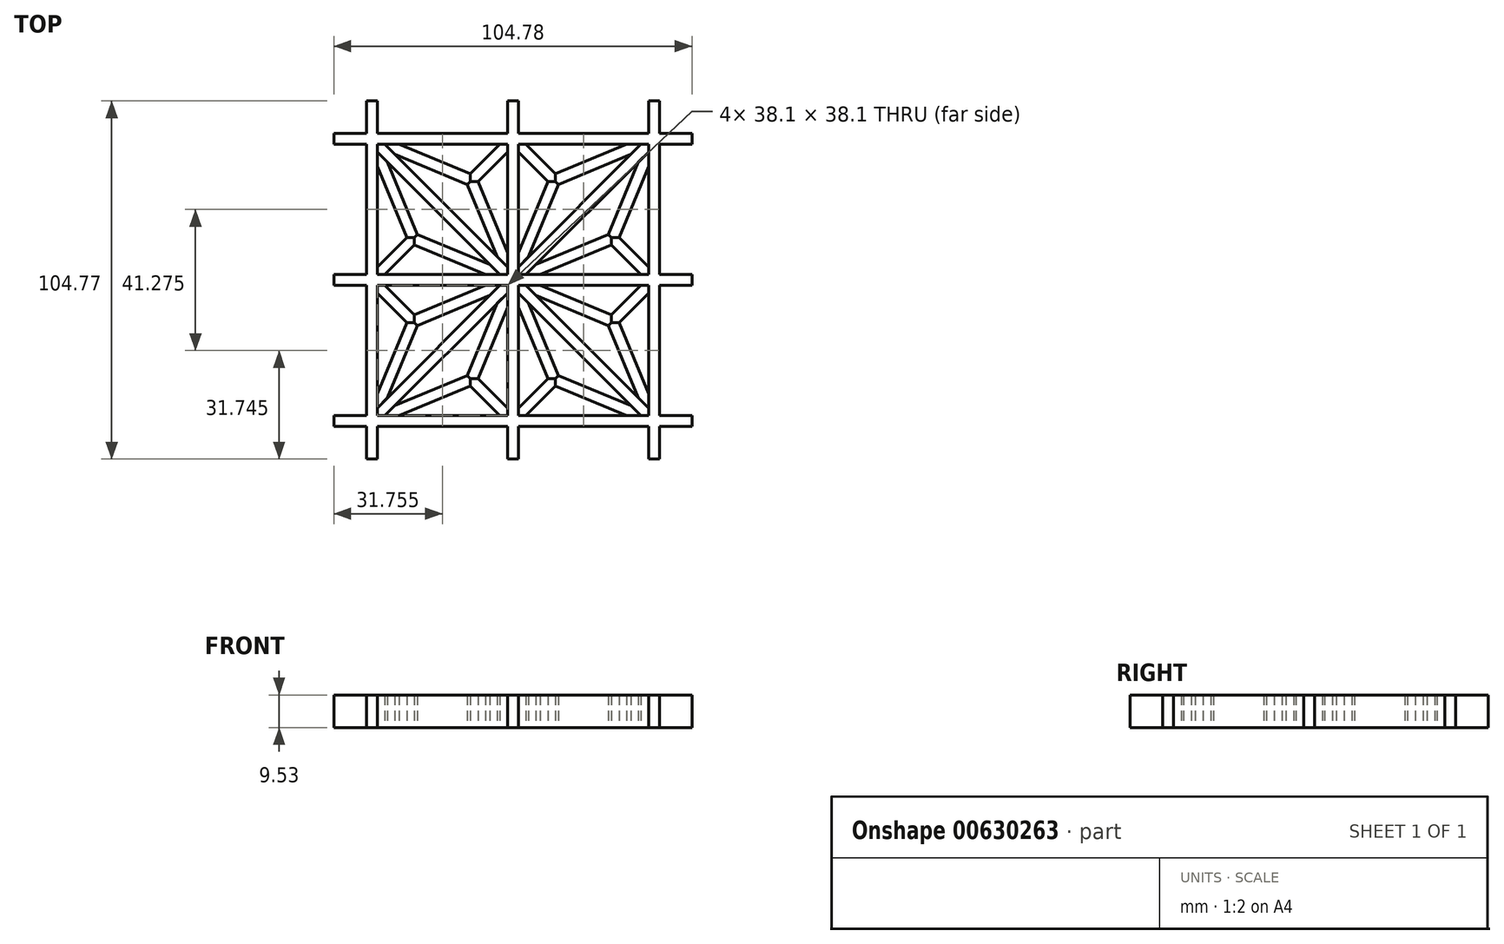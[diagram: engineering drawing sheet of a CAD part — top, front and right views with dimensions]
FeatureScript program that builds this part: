
annotation { "Feature Type Name" : "Feature", "Feature Type Description" : "" }
export const myFeature = defineFeature(function(context is Context, id is Id, definition is map)
    precondition{}
    {
        {
            var Q0;
            Q0=qCreatedBy(makeId("Top.planeOp"),FACE);
            var sketch = newSketch(context, id + "F0", { "sketchPlane" : qUnion([Q0])});
            skLineSegment(sketch, "E0.bottom", {"start": v(0, 0) * mm, "end": v(3.17, 0) * mm});
            skLineSegment(sketch, "E0.top", {"start": v(0, -104.78) * mm, "end": v(3.18, -104.78) * mm});
            skLineSegment(sketch, "E0.left", {"start": v(0, 0) * mm, "end": v(0, -104.78) * mm});
            skLineSegment(sketch, "E0.right", {"start": v(3.17, 0) * mm, "end": v(3.17, -104.78) * mm});
            skLineSegment(sketch, "E1.bottom", {"start": v(41.28, 0) * mm, "end": v(44.45, 0) * mm});
            skLineSegment(sketch, "E1.top", {"start": v(41.28, -104.78) * mm, "end": v(44.45, -104.78) * mm});
            skLineSegment(sketch, "E1.left", {"start": v(41.28, 0) * mm, "end": v(41.28, -104.78) * mm});
            skLineSegment(sketch, "E1.right", {"start": v(44.45, 0) * mm, "end": v(44.45, -104.78) * mm});
            skLineSegment(sketch, "E2.bottom", {"start": v(82.55, 0) * mm, "end": v(85.73, 0) * mm});
            skLineSegment(sketch, "E2.top", {"start": v(82.55, -104.78) * mm, "end": v(85.73, -104.78) * mm});
            skLineSegment(sketch, "E2.left", {"start": v(82.55, 0) * mm, "end": v(82.55, -104.78) * mm});
            skLineSegment(sketch, "E2.right", {"start": v(85.73, 0) * mm, "end": v(85.73, -104.78) * mm});
            skLineSegment(sketch, "E3", {"start": v(3.17, 0) * mm, "end": v(41.28, 0) * mm, "construction": true});
            skLineSegment(sketch, "E4", {"start": v(44.45, 0) * mm, "end": v(82.55, 0) * mm, "construction": true});
            skLineSegment(sketch, "E5", {"start": v(-9.53, -107.95) * mm, "end": v(95.25, -107.95) * mm, "construction": true});
            skLineSegment(sketch, "E6", {"start": v(0, -104.78) * mm, "end": v(-9.53, -104.78) * mm, "construction": true});
            skLineSegment(sketch, "E7", {"start": v(-9.52, -104.78) * mm, "end": v(-9.52, -107.95) * mm, "construction": true});
            skLineSegment(sketch, "E8", {"start": v(95.25, -107.95) * mm, "end": v(95.25, -104.78) * mm, "construction": true});
            skLineSegment(sketch, "E9", {"start": v(95.25, -104.78) * mm, "end": v(85.73, -104.78) * mm, "construction": true});
            skSolve(sketch);
        }
        {
            var Q0;
            Q0 = qSketchRegion(id + "F0", true);
            extrude(context, id + "F1", {"entities" : qUnion([Q0]), "depth" : 9.52 * mm, "offsetDistance" : 25.4 * mm});
        }
        {
            var Q0;
            Q0=makeQuery(id+"F1.opExtrude","SWEPT_FACE",FACE,{"disambiguationData":[OSD([sQuery(id+"F0.wireOp",EDGE,"E2.right")])]});
            var sketch = newSketch(context, id + "F2", { "sketchPlane" : qUnion([Q0])});
            skLineSegment(sketch, "E10.bottom", {"start": v(-95.25, 0) * mm, "end": v(-92.08, 0) * mm});
            skLineSegment(sketch, "E10.top", {"start": v(-95.25, 4.76) * mm, "end": v(-92.08, 4.76) * mm});
            skLineSegment(sketch, "E10.left", {"start": v(-95.25, 0) * mm, "end": v(-95.25, 4.76) * mm});
            skLineSegment(sketch, "E10.right", {"start": v(-92.08, 0) * mm, "end": v(-92.08, 4.76) * mm});
            skLineSegment(sketch, "E11.bottom", {"start": v(-53.98, 0) * mm, "end": v(-50.8, 0) * mm});
            skLineSegment(sketch, "E11.top", {"start": v(-53.98, 4.76) * mm, "end": v(-50.8, 4.76) * mm});
            skLineSegment(sketch, "E11.left", {"start": v(-50.8, 0) * mm, "end": v(-50.8, 4.76) * mm});
            skLineSegment(sketch, "E11.right", {"start": v(-53.98, 0) * mm, "end": v(-53.98, 4.76) * mm});
            skLineSegment(sketch, "E12.bottom", {"start": v(-12.7, 0) * mm, "end": v(-9.53, 0) * mm});
            skLineSegment(sketch, "E12.top", {"start": v(-12.7, 4.76) * mm, "end": v(-9.53, 4.76) * mm});
            skLineSegment(sketch, "E12.left", {"start": v(-12.7, 0) * mm, "end": v(-12.7, 4.76) * mm});
            skLineSegment(sketch, "E12.right", {"start": v(-9.53, 0) * mm, "end": v(-9.53, 4.76) * mm});
            skLineSegment(sketch, "E13", {"start": v(-52.39, 4.76) * mm, "end": v(-52.39, 9.52) * mm, "construction": true});
            skSolve(sketch);
        }
        {
            var Q0;
            Q0 = qSketchRegion(id + "F2", true);
            extrude(context, id + "F3", {"entities" : qUnion([Q0]), "operationType" : NewBodyOperationType.REMOVE, "endBound" : BoundingType.THROUGH_ALL, "oppositeDirection" : true, "depth" : 25.4 * mm, "offsetDistance" : 25.4 * mm});
        }
        {
            var Q0;
            Q0=qCreatedBy(makeId("Top.planeOp"),FACE);
            var sketch = newSketch(context, id + "F4", { "sketchPlane" : qUnion([Q0])});
            skLineSegment(sketch, "E14.bottom", {"start": v(95.25, -12.7) * mm, "end": v(-9.53, -12.7) * mm});
            skLineSegment(sketch, "E14.top", {"start": v(95.25, -9.53) * mm, "end": v(-9.53, -9.53) * mm});
            skLineSegment(sketch, "E14.left", {"start": v(95.25, -12.7) * mm, "end": v(95.25, -9.53) * mm});
            skLineSegment(sketch, "E14.right", {"start": v(-9.53, -12.7) * mm, "end": v(-9.53, -9.53) * mm});
            skLineSegment(sketch, "E15.bottom", {"start": v(95.25, -53.98) * mm, "end": v(-9.53, -53.98) * mm});
            skLineSegment(sketch, "E15.top", {"start": v(95.25, -50.8) * mm, "end": v(-9.53, -50.8) * mm});
            skLineSegment(sketch, "E15.left", {"start": v(95.25, -53.98) * mm, "end": v(95.25, -50.8) * mm});
            skLineSegment(sketch, "E15.right", {"start": v(-9.52, -53.98) * mm, "end": v(-9.52, -50.8) * mm});
            skLineSegment(sketch, "E16.bottom", {"start": v(95.25, -95.25) * mm, "end": v(-9.53, -95.25) * mm});
            skLineSegment(sketch, "E16.top", {"start": v(95.25, -92.08) * mm, "end": v(-9.53, -92.08) * mm});
            skLineSegment(sketch, "E16.left", {"start": v(95.25, -95.25) * mm, "end": v(95.25, -92.08) * mm});
            skLineSegment(sketch, "E16.right", {"start": v(-9.52, -95.25) * mm, "end": v(-9.52, -92.08) * mm});
            skLineSegment(sketch, "E17", {"start": v(42.86, -9.53) * mm, "end": v(42.86, 0) * mm, "construction": true});
            skSolve(sketch);
        }
        {
            var Q0;
            Q0 = qSketchRegion(id + "F4", true);
            var Q1;
            Q1=makeQuery(id+"F3.boolean.opBoolean","COPY",FACE,{"disambiguationData":[TD([makeQuery(id+"F1.opExtrude","SWEPT_FACE",FACE,{"disambiguationData":[OSD([sQuery(id+"F0.wireOp",EDGE,"E1.left")])]})])],"derivedFrom":makeQuery(id+"F3.opExtrude","SWEPT_FACE",FACE,{"disambiguationData":[OSD([sQuery(id+"F2.wireOp",EDGE,"E12.top")])]})});
            extrude(context, id + "F5", {"entities" : qUnion([Q0]), "endBound" : BoundingType.UP_TO_SURFACE, "depth" : 25.4 * mm, "endBoundEntityFace" : qUnion([Q1]), "offsetDistance" : 25.4 * mm});
        }
        {
            var Q0;
            Q0=makeQuery(id+"F5.opExtrude","CAP_FACE",FACE,{"disambiguationData":[OSD([sQuery(id+"F4.wireOp",EDGE,"E14.bottom"),sQuery(id+"F4.wireOp",EDGE,"E14.top"),sQuery(id+"F4.wireOp",EDGE,"E14.left"),sQuery(id+"F4.wireOp",EDGE,"E14.right")])],"isStart":false});
            var sketch = newSketch(context, id + "F6", { "sketchPlane" : qUnion([Q0])});
            skLineSegment(sketch, "E18.bottom", {"start": v(3.18, -9.53) * mm, "end": v(41.28, -9.53) * mm});
            skLineSegment(sketch, "E18.top", {"start": v(3.18, -12.7) * mm, "end": v(41.28, -12.7) * mm});
            skLineSegment(sketch, "E18.left", {"start": v(3.17, -9.53) * mm, "end": v(3.17, -12.7) * mm});
            skLineSegment(sketch, "E18.right", {"start": v(41.28, -9.53) * mm, "end": v(41.28, -12.7) * mm});
            skLineSegment(sketch, "E19.bottom", {"start": v(3.18, -50.8) * mm, "end": v(41.28, -50.8) * mm});
            skLineSegment(sketch, "E19.top", {"start": v(3.18, -53.98) * mm, "end": v(41.28, -53.98) * mm});
            skLineSegment(sketch, "E19.left", {"start": v(3.17, -50.8) * mm, "end": v(3.17, -53.98) * mm});
            skLineSegment(sketch, "E19.right", {"start": v(41.28, -50.8) * mm, "end": v(41.28, -53.98) * mm});
            skLineSegment(sketch, "E20.bottom", {"start": v(3.18, -92.08) * mm, "end": v(41.28, -92.08) * mm});
            skLineSegment(sketch, "E20.top", {"start": v(3.18, -95.25) * mm, "end": v(41.28, -95.25) * mm});
            skLineSegment(sketch, "E20.left", {"start": v(3.17, -92.08) * mm, "end": v(3.17, -95.25) * mm});
            skLineSegment(sketch, "E20.right", {"start": v(41.28, -92.08) * mm, "end": v(41.28, -95.25) * mm});
            skLineSegment(sketch, "E21.bottom", {"start": v(82.55, -95.25) * mm, "end": v(44.45, -95.25) * mm});
            skLineSegment(sketch, "E21.top", {"start": v(82.55, -92.08) * mm, "end": v(44.45, -92.08) * mm});
            skLineSegment(sketch, "E21.left", {"start": v(82.55, -95.25) * mm, "end": v(82.55, -92.08) * mm});
            skLineSegment(sketch, "E21.right", {"start": v(44.45, -95.25) * mm, "end": v(44.45, -92.08) * mm});
            skLineSegment(sketch, "E22.bottom", {"start": v(82.55, -53.98) * mm, "end": v(44.45, -53.98) * mm});
            skLineSegment(sketch, "E22.top", {"start": v(82.55, -50.8) * mm, "end": v(44.45, -50.8) * mm});
            skLineSegment(sketch, "E22.left", {"start": v(82.55, -53.98) * mm, "end": v(82.55, -50.8) * mm});
            skLineSegment(sketch, "E22.right", {"start": v(44.45, -53.98) * mm, "end": v(44.45, -50.8) * mm});
            skLineSegment(sketch, "E23.bottom", {"start": v(82.55, -9.53) * mm, "end": v(44.45, -9.53) * mm});
            skLineSegment(sketch, "E23.top", {"start": v(82.55, -12.7) * mm, "end": v(44.45, -12.7) * mm});
            skLineSegment(sketch, "E23.left", {"start": v(82.55, -9.53) * mm, "end": v(82.55, -12.7) * mm});
            skLineSegment(sketch, "E23.right", {"start": v(44.45, -9.53) * mm, "end": v(44.45, -12.7) * mm});
            skLineSegment(sketch, "E24.bottom", {"start": v(95.25, -9.53) * mm, "end": v(85.73, -9.53) * mm});
            skLineSegment(sketch, "E24.top", {"start": v(95.25, -12.7) * mm, "end": v(85.73, -12.7) * mm});
            skLineSegment(sketch, "E24.left", {"start": v(95.25, -9.53) * mm, "end": v(95.25, -12.7) * mm});
            skLineSegment(sketch, "E24.right", {"start": v(85.73, -9.53) * mm, "end": v(85.73, -12.7) * mm});
            skLineSegment(sketch, "E25.bottom", {"start": v(95.25, -50.8) * mm, "end": v(85.73, -50.8) * mm});
            skLineSegment(sketch, "E25.top", {"start": v(95.25, -53.98) * mm, "end": v(85.73, -53.98) * mm});
            skLineSegment(sketch, "E25.left", {"start": v(95.25, -50.8) * mm, "end": v(95.25, -53.98) * mm});
            skLineSegment(sketch, "E25.right", {"start": v(85.73, -50.8) * mm, "end": v(85.73, -53.98) * mm});
            skLineSegment(sketch, "E26.bottom", {"start": v(95.25, -92.08) * mm, "end": v(85.73, -92.08) * mm});
            skLineSegment(sketch, "E26.top", {"start": v(95.25, -95.25) * mm, "end": v(85.73, -95.25) * mm});
            skLineSegment(sketch, "E26.left", {"start": v(95.25, -92.08) * mm, "end": v(95.25, -95.25) * mm});
            skLineSegment(sketch, "E26.right", {"start": v(85.73, -92.08) * mm, "end": v(85.73, -95.25) * mm});
            skLineSegment(sketch, "E27.bottom", {"start": v(0, -92.08) * mm, "end": v(-9.52, -92.08) * mm});
            skLineSegment(sketch, "E27.top", {"start": v(0, -95.25) * mm, "end": v(-9.52, -95.25) * mm});
            skLineSegment(sketch, "E27.left", {"start": v(0, -92.08) * mm, "end": v(0, -95.25) * mm});
            skLineSegment(sketch, "E27.right", {"start": v(-9.52, -92.08) * mm, "end": v(-9.52, -95.25) * mm});
            skLineSegment(sketch, "E28.bottom", {"start": v(0, -50.8) * mm, "end": v(-9.52, -50.8) * mm});
            skLineSegment(sketch, "E28.top", {"start": v(0, -53.98) * mm, "end": v(-9.52, -53.98) * mm});
            skLineSegment(sketch, "E28.left", {"start": v(0, -50.8) * mm, "end": v(0, -53.98) * mm});
            skLineSegment(sketch, "E28.right", {"start": v(-9.52, -50.8) * mm, "end": v(-9.52, -53.98) * mm});
            skLineSegment(sketch, "E29.bottom", {"start": v(0, -9.53) * mm, "end": v(-9.53, -9.53) * mm});
            skLineSegment(sketch, "E29.top", {"start": v(0, -12.7) * mm, "end": v(-9.53, -12.7) * mm});
            skLineSegment(sketch, "E29.left", {"start": v(0, -9.53) * mm, "end": v(0, -12.7) * mm});
            skLineSegment(sketch, "E29.right", {"start": v(-9.53, -9.53) * mm, "end": v(-9.53, -12.7) * mm});
            skSolve(sketch);
        }
        {
            var Q0;
            Q0 = qSketchRegion(id + "F6", true);
            var Q1;
            Q1=makeQuery(id+"F1.opExtrude","CAP_FACE",FACE,{"disambiguationData":[OSD([sQuery(id+"F0.wireOp",EDGE,"E1.bottom"),sQuery(id+"F0.wireOp",EDGE,"E1.top"),sQuery(id+"F0.wireOp",EDGE,"E1.left"),sQuery(id+"F0.wireOp",EDGE,"E1.right")])],"isStart":false});
            extrude(context, id + "F7", {"entities" : qUnion([Q0]), "operationType" : NewBodyOperationType.ADD, "endBound" : BoundingType.UP_TO_SURFACE, "depth" : 25.4 * mm, "endBoundEntityFace" : qUnion([Q1]), "offsetDistance" : 25.4 * mm});
        }
        {
            var Q0;
            Q0=qCreatedBy(makeId("Top.planeOp"),FACE);
            var sketch = newSketch(context, id + "F8", { "sketchPlane" : qUnion([Q0])});
            skLineSegment(sketch, "E30", {"start": v(46.7, -53.98) * mm, "end": v(44.45, -53.98) * mm});
            skLineSegment(sketch, "E31", {"start": v(44.45, -53.98) * mm, "end": v(44.45, -56.22) * mm});
            skLineSegment(sketch, "E32", {"start": v(44.45, -56.22) * mm, "end": v(80.3, -92.08) * mm});
            skLineSegment(sketch, "E33", {"start": v(80.3, -92.08) * mm, "end": v(82.55, -92.08) * mm});
            skLineSegment(sketch, "E34", {"start": v(82.55, -14.95) * mm, "end": v(46.7, -50.8) * mm});
            skLineSegment(sketch, "E35", {"start": v(46.7, -50.8) * mm, "end": v(44.45, -50.8) * mm});
            skLineSegment(sketch, "E36", {"start": v(44.45, -50.8) * mm, "end": v(44.45, -48.55) * mm});
            skLineSegment(sketch, "E37", {"start": v(44.45, -48.55) * mm, "end": v(80.3, -12.7) * mm});
            skLineSegment(sketch, "E38", {"start": v(80.3, -12.7) * mm, "end": v(82.55, -12.7) * mm});
            skLineSegment(sketch, "E39", {"start": v(82.55, -12.7) * mm, "end": v(82.55, -14.95) * mm});
            skLineSegment(sketch, "E40", {"start": v(41.28, -50.8) * mm, "end": v(41.28, -48.55) * mm});
            skLineSegment(sketch, "E41", {"start": v(41.28, -48.55) * mm, "end": v(5.42, -12.7) * mm});
            skLineSegment(sketch, "E42", {"start": v(5.42, -12.7) * mm, "end": v(3.17, -12.7) * mm});
            skLineSegment(sketch, "E43", {"start": v(3.17, -12.7) * mm, "end": v(3.17, -14.95) * mm});
            skLineSegment(sketch, "E44", {"start": v(3.17, -14.95) * mm, "end": v(39.03, -50.8) * mm});
            skLineSegment(sketch, "E45", {"start": v(39.03, -50.8) * mm, "end": v(41.28, -50.8) * mm});
            skLineSegment(sketch, "E46", {"start": v(41.28, -56.22) * mm, "end": v(41.28, -53.98) * mm});
            skLineSegment(sketch, "E47", {"start": v(41.28, -53.98) * mm, "end": v(39.03, -53.98) * mm});
            skLineSegment(sketch, "E48", {"start": v(39.03, -53.97) * mm, "end": v(3.17, -89.83) * mm});
            skLineSegment(sketch, "E49", {"start": v(3.17, -89.83) * mm, "end": v(3.18, -92.08) * mm});
            skLineSegment(sketch, "E50", {"start": v(3.18, -92.08) * mm, "end": v(5.42, -92.08) * mm});
            skLineSegment(sketch, "E51", {"start": v(5.42, -92.08) * mm, "end": v(41.28, -56.22) * mm});
            skLineSegment(sketch, "E52", {"start": v(82.55, -92.08) * mm, "end": v(82.55, -89.83) * mm});
            skLineSegment(sketch, "E53", {"start": v(82.55, -89.83) * mm, "end": v(46.7, -53.97) * mm});
            skSolve(sketch);
        }
        {
            var Q0;
            Q0 = qSketchRegion(id + "F8", true);
            var Q1;
            Q1=makeQuery(id+"F1.opExtrude","CAP_FACE",FACE,{"disambiguationData":[OSD([sQuery(id+"F0.wireOp",EDGE,"E1.bottom"),sQuery(id+"F0.wireOp",EDGE,"E1.top"),sQuery(id+"F0.wireOp",EDGE,"E1.left"),sQuery(id+"F0.wireOp",EDGE,"E1.right")])],"isStart":false});
            extrude(context, id + "F9", {"entities" : qUnion([Q0]), "endBound" : BoundingType.UP_TO_SURFACE, "depth" : 25.4 * mm, "endBoundEntityFace" : qUnion([Q1]), "offsetDistance" : 25.4 * mm});
        }
        {
            var Q0;
            Q0=qCreatedBy(makeId("Top.planeOp"),FACE);
            var sketch = newSketch(context, id + "F10", { "sketchPlane" : qUnion([Q0])});
            skLineSegment(sketch, "E54", {"start": v(46.7, -12.7) * mm, "end": v(55.32, -21.33) * mm});
            skLineSegment(sketch, "E55", {"start": v(55.32, -21.33) * mm, "end": v(55.32, -23.57) * mm});
            skLineSegment(sketch, "E56", {"start": v(55.32, -23.57) * mm, "end": v(53.08, -23.57) * mm});
            skLineSegment(sketch, "E57", {"start": v(53.08, -23.57) * mm, "end": v(44.45, -14.95) * mm});
            skLineSegment(sketch, "E58", {"start": v(44.45, -14.95) * mm, "end": v(44.45, -12.7) * mm});
            skLineSegment(sketch, "E59", {"start": v(44.45, -12.7) * mm, "end": v(46.7, -12.7) * mm});
            skLineSegment(sketch, "E60", {"start": v(73.92, -39.93) * mm, "end": v(82.55, -48.55) * mm});
            skLineSegment(sketch, "E61", {"start": v(82.55, -48.55) * mm, "end": v(82.55, -50.8) * mm});
            skLineSegment(sketch, "E62", {"start": v(82.55, -50.8) * mm, "end": v(80.3, -50.8) * mm});
            skLineSegment(sketch, "E63", {"start": v(80.3, -50.8) * mm, "end": v(71.68, -42.17) * mm});
            skLineSegment(sketch, "E64", {"start": v(71.68, -42.17) * mm, "end": v(71.68, -39.93) * mm});
            skLineSegment(sketch, "E65", {"start": v(71.68, -39.93) * mm, "end": v(73.92, -39.93) * mm});
            skLineSegment(sketch, "E66", {"start": v(55.32, -23.57) * mm, "end": v(56.17, -24.42) * mm});
            skLineSegment(sketch, "E67", {"start": v(71.68, -39.93) * mm, "end": v(70.83, -39.08) * mm});
            skLineSegment(sketch, "E68", {"start": v(47.38, -45.62) * mm, "end": v(44.45, -48.55) * mm});
            skLineSegment(sketch, "E69", {"start": v(44.45, -48.55) * mm, "end": v(44.45, -44.4) * mm});
            skLineSegment(sketch, "E70", {"start": v(80.3, -12.7) * mm, "end": v(76.16, -12.7) * mm});
            skLineSegment(sketch, "E71", {"start": v(77.37, -15.63) * mm, "end": v(80.3, -12.7) * mm});
            skLineSegment(sketch, "E72", {"start": v(56.17, -24.42) * mm, "end": v(47.38, -45.62) * mm});
            skLineSegment(sketch, "E73", {"start": v(53.08, -23.57) * mm, "end": v(44.45, -44.4) * mm});
            skLineSegment(sketch, "E74", {"start": v(56.17, -24.42) * mm, "end": v(77.37, -15.63) * mm});
            skLineSegment(sketch, "E75", {"start": v(76.16, -12.7) * mm, "end": v(55.32, -21.33) * mm});
            skLineSegment(sketch, "E76", {"start": v(47.38, -41.47) * mm, "end": v(50.32, -42.69) * mm, "construction": true});
            skLineSegment(sketch, "E77", {"start": v(47.38, -41.47) * mm, "end": v(44.45, -40.26) * mm, "construction": true});
            skLineSegment(sketch, "E78", {"start": v(47.38, -45.62) * mm, "end": v(47.38, -41.47) * mm, "construction": true});
            skLineSegment(sketch, "E79", {"start": v(47.38, -41.47) * mm, "end": v(44.45, -44.4) * mm, "construction": true});
            skLineSegment(sketch, "E80", {"start": v(70.83, -39.08) * mm, "end": v(49.63, -47.87) * mm});
            skLineSegment(sketch, "E81", {"start": v(49.63, -47.87) * mm, "end": v(46.7, -50.8) * mm});
            skLineSegment(sketch, "E82", {"start": v(46.7, -50.8) * mm, "end": v(50.84, -50.8) * mm});
            skLineSegment(sketch, "E83", {"start": v(50.84, -50.8) * mm, "end": v(71.68, -42.17) * mm});
            skLineSegment(sketch, "E84", {"start": v(70.83, -39.08) * mm, "end": v(79.62, -17.88) * mm});
            skLineSegment(sketch, "E85", {"start": v(79.62, -17.88) * mm, "end": v(82.55, -14.95) * mm});
            skLineSegment(sketch, "E86", {"start": v(82.55, -14.95) * mm, "end": v(82.55, -19.1) * mm});
            skLineSegment(sketch, "E87", {"start": v(82.55, -19.1) * mm, "end": v(73.92, -39.93) * mm});
            skLineSegment(sketch, "E88", {"start": v(5.42, -53.97) * mm, "end": v(14.05, -62.6) * mm});
            skLineSegment(sketch, "E89", {"start": v(14.05, -62.6) * mm, "end": v(14.05, -64.85) * mm});
            skLineSegment(sketch, "E90", {"start": v(14.05, -64.85) * mm, "end": v(11.8, -64.85) * mm});
            skLineSegment(sketch, "E91", {"start": v(11.8, -64.85) * mm, "end": v(3.17, -56.22) * mm});
            skLineSegment(sketch, "E92", {"start": v(3.17, -56.22) * mm, "end": v(3.17, -53.98) * mm});
            skLineSegment(sketch, "E93", {"start": v(3.17, -53.97) * mm, "end": v(5.42, -53.97) * mm});
            skLineSegment(sketch, "E94", {"start": v(32.65, -81.2) * mm, "end": v(41.27, -89.83) * mm});
            skLineSegment(sketch, "E95", {"start": v(41.28, -89.83) * mm, "end": v(41.28, -92.08) * mm});
            skLineSegment(sketch, "E96", {"start": v(41.28, -92.08) * mm, "end": v(39.03, -92.08) * mm});
            skLineSegment(sketch, "E97", {"start": v(39.03, -92.08) * mm, "end": v(30.4, -83.45) * mm});
            skLineSegment(sketch, "E98", {"start": v(30.4, -83.45) * mm, "end": v(30.4, -81.2) * mm});
            skLineSegment(sketch, "E99", {"start": v(30.4, -81.2) * mm, "end": v(32.65, -81.2) * mm});
            skLineSegment(sketch, "E100", {"start": v(14.05, -64.85) * mm, "end": v(14.9, -65.7) * mm});
            skLineSegment(sketch, "E101", {"start": v(30.4, -81.2) * mm, "end": v(29.56, -80.36) * mm});
            skLineSegment(sketch, "E102", {"start": v(6.1, -86.9) * mm, "end": v(3.18, -89.83) * mm});
            skLineSegment(sketch, "E103", {"start": v(3.17, -89.83) * mm, "end": v(3.17, -85.68) * mm});
            skLineSegment(sketch, "E104", {"start": v(39.03, -53.98) * mm, "end": v(34.88, -53.98) * mm});
            skLineSegment(sketch, "E105", {"start": v(36.1, -56.9) * mm, "end": v(39.03, -53.98) * mm});
            skLineSegment(sketch, "E106", {"start": v(14.9, -65.7) * mm, "end": v(6.1, -86.9) * mm});
            skLineSegment(sketch, "E107", {"start": v(11.8, -64.85) * mm, "end": v(3.18, -85.68) * mm});
            skLineSegment(sketch, "E108", {"start": v(14.9, -65.7) * mm, "end": v(36.1, -56.9) * mm});
            skLineSegment(sketch, "E109", {"start": v(34.88, -53.98) * mm, "end": v(14.05, -62.6) * mm});
            skLineSegment(sketch, "E110", {"start": v(6.1, -86.9) * mm, "end": v(6.1, -82.75) * mm, "construction": true});
            skLineSegment(sketch, "E111", {"start": v(6.1, -82.75) * mm, "end": v(3.17, -85.68) * mm, "construction": true});
            skLineSegment(sketch, "E112", {"start": v(29.56, -80.36) * mm, "end": v(8.35, -89.14) * mm});
            skLineSegment(sketch, "E113", {"start": v(8.35, -89.14) * mm, "end": v(5.42, -92.08) * mm});
            skLineSegment(sketch, "E114", {"start": v(5.42, -92.08) * mm, "end": v(9.57, -92.08) * mm});
            skLineSegment(sketch, "E115", {"start": v(9.57, -92.08) * mm, "end": v(30.4, -83.45) * mm});
            skLineSegment(sketch, "E116", {"start": v(29.56, -80.36) * mm, "end": v(38.34, -59.15) * mm});
            skLineSegment(sketch, "E117", {"start": v(38.34, -59.15) * mm, "end": v(41.28, -56.22) * mm});
            skLineSegment(sketch, "E118", {"start": v(41.28, -56.22) * mm, "end": v(41.28, -60.37) * mm});
            skLineSegment(sketch, "E119", {"start": v(41.28, -60.37) * mm, "end": v(32.65, -81.2) * mm});
            skLineSegment(sketch, "E120", {"start": v(3.17, -81.53) * mm, "end": v(6.1, -82.75) * mm, "construction": true});
            skLineSegment(sketch, "E121", {"start": v(9.04, -83.96) * mm, "end": v(6.1, -82.75) * mm, "construction": true});
            skLineSegment(sketch, "E122", {"start": v(41.28, -12.7) * mm, "end": v(39.03, -12.7) * mm});
            skLineSegment(sketch, "E123", {"start": v(39.03, -12.7) * mm, "end": v(30.4, -21.33) * mm});
            skLineSegment(sketch, "E124", {"start": v(30.4, -21.33) * mm, "end": v(30.4, -23.57) * mm});
            skLineSegment(sketch, "E125", {"start": v(30.4, -23.57) * mm, "end": v(32.65, -23.57) * mm});
            skLineSegment(sketch, "E126", {"start": v(32.65, -23.57) * mm, "end": v(41.28, -14.95) * mm});
            skLineSegment(sketch, "E127", {"start": v(41.28, -14.95) * mm, "end": v(41.28, -12.7) * mm});
            skLineSegment(sketch, "E128", {"start": v(38.34, -45.62) * mm, "end": v(41.28, -48.55) * mm});
            skLineSegment(sketch, "E129", {"start": v(41.28, -48.55) * mm, "end": v(41.28, -44.4) * mm});
            skLineSegment(sketch, "E130", {"start": v(41.28, -44.4) * mm, "end": v(32.65, -23.57) * mm});
            skLineSegment(sketch, "E131", {"start": v(30.4, -23.57) * mm, "end": v(29.56, -24.42) * mm});
            skLineSegment(sketch, "E132", {"start": v(29.56, -24.42) * mm, "end": v(38.34, -45.62) * mm});
            skLineSegment(sketch, "E133", {"start": v(29.56, -24.42) * mm, "end": v(8.35, -15.63) * mm});
            skLineSegment(sketch, "E134", {"start": v(8.35, -15.63) * mm, "end": v(5.42, -12.7) * mm});
            skLineSegment(sketch, "E135", {"start": v(5.42, -12.7) * mm, "end": v(9.57, -12.7) * mm});
            skLineSegment(sketch, "E136", {"start": v(9.57, -12.7) * mm, "end": v(30.4, -21.33) * mm});
            skLineSegment(sketch, "E137", {"start": v(3.17, -19.1) * mm, "end": v(3.17, -14.95) * mm});
            skLineSegment(sketch, "E138", {"start": v(3.18, -14.95) * mm, "end": v(6.1, -17.88) * mm});
            skLineSegment(sketch, "E139", {"start": v(6.1, -17.88) * mm, "end": v(14.9, -39.08) * mm});
            skLineSegment(sketch, "E140", {"start": v(14.9, -39.08) * mm, "end": v(36.1, -47.87) * mm});
            skLineSegment(sketch, "E141", {"start": v(36.1, -47.87) * mm, "end": v(39.03, -50.8) * mm});
            skLineSegment(sketch, "E142", {"start": v(39.03, -50.8) * mm, "end": v(34.88, -50.8) * mm});
            skLineSegment(sketch, "E143", {"start": v(34.88, -50.8) * mm, "end": v(14.05, -42.17) * mm});
            skLineSegment(sketch, "E144", {"start": v(14.05, -42.17) * mm, "end": v(14.05, -39.93) * mm});
            skLineSegment(sketch, "E145", {"start": v(14.05, -39.93) * mm, "end": v(14.9, -39.08) * mm});
            skLineSegment(sketch, "E146", {"start": v(3.17, -19.1) * mm, "end": v(11.8, -39.93) * mm});
            skLineSegment(sketch, "E147", {"start": v(11.8, -39.93) * mm, "end": v(14.05, -39.93) * mm});
            skLineSegment(sketch, "E148", {"start": v(11.8, -39.93) * mm, "end": v(3.18, -48.55) * mm});
            skLineSegment(sketch, "E149", {"start": v(3.17, -48.55) * mm, "end": v(3.18, -50.8) * mm});
            skLineSegment(sketch, "E150", {"start": v(3.18, -50.8) * mm, "end": v(5.42, -50.8) * mm});
            skLineSegment(sketch, "E151", {"start": v(5.42, -50.8) * mm, "end": v(14.05, -42.17) * mm});
            skLineSegment(sketch, "E152", {"start": v(80.3, -53.98) * mm, "end": v(82.55, -53.98) * mm});
            skLineSegment(sketch, "E153", {"start": v(82.55, -53.98) * mm, "end": v(82.55, -56.22) * mm});
            skLineSegment(sketch, "E154", {"start": v(82.55, -56.22) * mm, "end": v(73.92, -64.85) * mm});
            skLineSegment(sketch, "E155", {"start": v(73.92, -64.85) * mm, "end": v(71.68, -64.85) * mm});
            skLineSegment(sketch, "E156", {"start": v(71.68, -64.85) * mm, "end": v(71.68, -62.6) * mm});
            skLineSegment(sketch, "E157", {"start": v(71.68, -62.6) * mm, "end": v(80.3, -53.97) * mm});
            skLineSegment(sketch, "E158", {"start": v(73.92, -64.85) * mm, "end": v(82.55, -85.68) * mm});
            skLineSegment(sketch, "E159", {"start": v(82.55, -85.68) * mm, "end": v(82.55, -89.83) * mm});
            skLineSegment(sketch, "E160", {"start": v(82.55, -89.83) * mm, "end": v(79.62, -86.9) * mm});
            skLineSegment(sketch, "E161", {"start": v(79.62, -86.9) * mm, "end": v(70.83, -65.7) * mm});
            skLineSegment(sketch, "E162", {"start": v(70.83, -65.7) * mm, "end": v(71.68, -64.85) * mm});
            skLineSegment(sketch, "E163", {"start": v(70.83, -65.7) * mm, "end": v(49.63, -56.9) * mm});
            skLineSegment(sketch, "E164", {"start": v(49.63, -56.9) * mm, "end": v(46.7, -53.98) * mm});
            skLineSegment(sketch, "E165", {"start": v(46.7, -53.98) * mm, "end": v(50.84, -53.98) * mm});
            skLineSegment(sketch, "E166", {"start": v(50.84, -53.98) * mm, "end": v(71.68, -62.6) * mm});
            skLineSegment(sketch, "E167", {"start": v(44.45, -56.22) * mm, "end": v(47.38, -59.15) * mm});
            skLineSegment(sketch, "E168", {"start": v(47.38, -59.15) * mm, "end": v(56.17, -80.36) * mm});
            skLineSegment(sketch, "E169", {"start": v(56.17, -80.36) * mm, "end": v(77.37, -89.14) * mm});
            skLineSegment(sketch, "E170", {"start": v(77.37, -89.14) * mm, "end": v(80.3, -92.08) * mm});
            skLineSegment(sketch, "E171", {"start": v(80.3, -92.08) * mm, "end": v(76.16, -92.08) * mm});
            skLineSegment(sketch, "E172", {"start": v(76.16, -92.08) * mm, "end": v(55.32, -83.45) * mm});
            skLineSegment(sketch, "E173", {"start": v(55.32, -83.45) * mm, "end": v(55.32, -81.2) * mm});
            skLineSegment(sketch, "E174", {"start": v(55.32, -81.2) * mm, "end": v(56.17, -80.36) * mm});
            skLineSegment(sketch, "E175", {"start": v(44.45, -56.22) * mm, "end": v(44.45, -60.37) * mm});
            skLineSegment(sketch, "E176", {"start": v(44.45, -60.37) * mm, "end": v(53.08, -81.2) * mm});
            skLineSegment(sketch, "E177", {"start": v(53.08, -81.2) * mm, "end": v(55.32, -81.2) * mm});
            skLineSegment(sketch, "E178", {"start": v(53.08, -81.2) * mm, "end": v(44.45, -89.83) * mm});
            skLineSegment(sketch, "E179", {"start": v(44.45, -89.83) * mm, "end": v(44.45, -92.08) * mm});
            skLineSegment(sketch, "E180", {"start": v(44.45, -92.08) * mm, "end": v(46.7, -92.08) * mm});
            skLineSegment(sketch, "E181", {"start": v(46.7, -92.08) * mm, "end": v(55.32, -83.45) * mm});
            skSolve(sketch);
        }
        {
            var Q0;
            Q0=makeQuery(id+"F10.imprint","IMPRINT",FACE,{"disambiguationData":[TD([[makeQuery(id+"F10.imprint","IMPRINT",EDGE,{"derivedFrom":sQuery(id+"F10.wireOp",EDGE,"E55")}),1.0]])]});
            var Q1;
            Q1=makeQuery(id+"F10.imprint","IMPRINT",FACE,{"disambiguationData":[TD([[makeQuery(id+"F10.imprint","IMPRINT",EDGE,{"derivedFrom":sQuery(id+"F10.wireOp",EDGE,"E65")}),1.0]])]});
            var Q2;
            Q2=makeQuery(id+"F10.imprint","IMPRINT",FACE,{"disambiguationData":[TD([[makeQuery(id+"F10.imprint","IMPRINT",EDGE,{"derivedFrom":sQuery(id+"F10.wireOp",EDGE,"E155")}),1.0]])]});
            var Q3;
            Q3=makeQuery(id+"F10.imprint","IMPRINT",FACE,{"disambiguationData":[TD([[makeQuery(id+"F10.imprint","IMPRINT",EDGE,{"derivedFrom":sQuery(id+"F10.wireOp",EDGE,"E169")}),-1.0]])]});
            var Q4;
            Q4=makeQuery(id+"F10.imprint","IMPRINT",FACE,{"disambiguationData":[TD([[makeQuery(id+"F10.imprint","IMPRINT",EDGE,{"derivedFrom":sQuery(id+"F10.wireOp",EDGE,"E98")}),1.0]])]});
            var Q5;
            Q5=makeQuery(id+"F10.imprint","IMPRINT",FACE,{"disambiguationData":[TD([[makeQuery(id+"F10.imprint","IMPRINT",EDGE,{"derivedFrom":sQuery(id+"F10.wireOp",EDGE,"E90")}),1.0]])]});
            var Q6;
            Q6=makeQuery(id+"F10.imprint","IMPRINT",FACE,{"disambiguationData":[TD([[makeQuery(id+"F10.imprint","IMPRINT",EDGE,{"derivedFrom":sQuery(id+"F10.wireOp",EDGE,"E137")}),-1.0]])]});
            var Q7;
            Q7=makeQuery(id+"F10.imprint","IMPRINT",FACE,{"disambiguationData":[TD([[makeQuery(id+"F10.imprint","IMPRINT",EDGE,{"derivedFrom":sQuery(id+"F10.wireOp",EDGE,"E124")}),-1.0]])]});
            var Q8;
            Q8=makeQuery(id+"F1.opExtrude","CAP_FACE",FACE,{"disambiguationData":[OSD([sQuery(id+"F0.wireOp",EDGE,"E1.bottom"),sQuery(id+"F0.wireOp",EDGE,"E1.top"),sQuery(id+"F0.wireOp",EDGE,"E1.left"),sQuery(id+"F0.wireOp",EDGE,"E1.right")])],"isStart":false});
            extrude(context, id + "F11", {"entities" : qUnion([Q0, Q1, Q2, Q3, Q4, Q5, Q6, Q7]), "endBound" : BoundingType.UP_TO_SURFACE, "depth" : 25.4 * mm, "endBoundEntityFace" : qUnion([Q8]), "offsetDistance" : 25.4 * mm});
        }
        {
            var Q0;
            Q0=makeQuery(id+"F10.imprint","IMPRINT",FACE,{"disambiguationData":[TD([[makeQuery(id+"F10.imprint","IMPRINT",EDGE,{"derivedFrom":sQuery(id+"F10.wireOp",EDGE,"E56")}),1.0]])]});
            var Q1;
            Q1=makeQuery(id+"F10.imprint","IMPRINT",FACE,{"disambiguationData":[TD([[makeQuery(id+"F10.imprint","IMPRINT",EDGE,{"derivedFrom":sQuery(id+"F10.wireOp",EDGE,"E64")}),1.0]])]});
            var Q2;
            Q2=makeQuery(id+"F10.imprint","IMPRINT",FACE,{"disambiguationData":[TD([[makeQuery(id+"F10.imprint","IMPRINT",EDGE,{"derivedFrom":sQuery(id+"F10.wireOp",EDGE,"E156")}),1.0]])]});
            var Q3;
            Q3=makeQuery(id+"F10.imprint","IMPRINT",FACE,{"disambiguationData":[TD([[makeQuery(id+"F10.imprint","IMPRINT",EDGE,{"derivedFrom":sQuery(id+"F10.wireOp",EDGE,"E167")}),-1.0]])]});
            var Q4;
            Q4=makeQuery(id+"F10.imprint","IMPRINT",FACE,{"disambiguationData":[TD([[makeQuery(id+"F10.imprint","IMPRINT",EDGE,{"derivedFrom":sQuery(id+"F10.wireOp",EDGE,"E99")}),1.0]])]});
            var Q5;
            Q5=makeQuery(id+"F10.imprint","IMPRINT",FACE,{"disambiguationData":[TD([[makeQuery(id+"F10.imprint","IMPRINT",EDGE,{"derivedFrom":sQuery(id+"F10.wireOp",EDGE,"E89")}),1.0]])]});
            var Q6;
            Q6=makeQuery(id+"F10.imprint","IMPRINT",FACE,{"disambiguationData":[TD([[makeQuery(id+"F10.imprint","IMPRINT",EDGE,{"derivedFrom":sQuery(id+"F10.wireOp",EDGE,"E140")}),-1.0]])]});
            var Q7;
            Q7=makeQuery(id+"F10.imprint","IMPRINT",FACE,{"disambiguationData":[TD([[makeQuery(id+"F10.imprint","IMPRINT",EDGE,{"derivedFrom":sQuery(id+"F10.wireOp",EDGE,"E125")}),-1.0]])]});
            var Q8;
            Q8=makeQuery(id+"F1.opExtrude","CAP_FACE",FACE,{"disambiguationData":[OSD([sQuery(id+"F0.wireOp",EDGE,"E1.bottom"),sQuery(id+"F0.wireOp",EDGE,"E1.top"),sQuery(id+"F0.wireOp",EDGE,"E1.left"),sQuery(id+"F0.wireOp",EDGE,"E1.right")])],"isStart":false});
            extrude(context, id + "F12", {"entities" : qUnion([Q0, Q1, Q2, Q3, Q4, Q5, Q6, Q7]), "endBound" : BoundingType.UP_TO_SURFACE, "depth" : 25.4 * mm, "endBoundEntityFace" : qUnion([Q8]), "offsetDistance" : 25.4 * mm});
        }
        {
            var Q0;
            Q0=makeQuery(id+"F10.imprint","IMPRINT",FACE,{"disambiguationData":[TD([[makeQuery(id+"F10.imprint","IMPRINT",EDGE,{"derivedFrom":sQuery(id+"F10.wireOp",EDGE,"E54")}),-1.0]])]});
            var Q1;
            Q1=makeQuery(id+"F10.imprint","IMPRINT",FACE,{"disambiguationData":[TD([[makeQuery(id+"F10.imprint","IMPRINT",EDGE,{"derivedFrom":sQuery(id+"F10.wireOp",EDGE,"E60")}),-1.0]])]});
            var Q2;
            Q2=makeQuery(id+"F10.imprint","IMPRINT",FACE,{"disambiguationData":[TD([[makeQuery(id+"F10.imprint","IMPRINT",EDGE,{"derivedFrom":sQuery(id+"F10.wireOp",EDGE,"E152")}),-1.0]])]});
            var Q3;
            Q3=makeQuery(id+"F10.imprint","IMPRINT",FACE,{"disambiguationData":[TD([[makeQuery(id+"F10.imprint","IMPRINT",EDGE,{"derivedFrom":sQuery(id+"F10.wireOp",EDGE,"E173")}),1.0]])]});
            var Q4;
            Q4=makeQuery(id+"F10.imprint","IMPRINT",FACE,{"disambiguationData":[TD([[makeQuery(id+"F10.imprint","IMPRINT",EDGE,{"derivedFrom":sQuery(id+"F10.wireOp",EDGE,"E94")}),-1.0]])]});
            var Q5;
            Q5=makeQuery(id+"F10.imprint","IMPRINT",FACE,{"disambiguationData":[TD([[makeQuery(id+"F10.imprint","IMPRINT",EDGE,{"derivedFrom":sQuery(id+"F10.wireOp",EDGE,"E88")}),-1.0]])]});
            var Q6;
            Q6=makeQuery(id+"F10.imprint","IMPRINT",FACE,{"disambiguationData":[TD([[makeQuery(id+"F10.imprint","IMPRINT",EDGE,{"derivedFrom":sQuery(id+"F10.wireOp",EDGE,"E144")}),1.0]])]});
            var Q7;
            Q7=makeQuery(id+"F10.imprint","IMPRINT",FACE,{"disambiguationData":[TD([[makeQuery(id+"F10.imprint","IMPRINT",EDGE,{"derivedFrom":sQuery(id+"F10.wireOp",EDGE,"E122")}),1.0]])]});
            var Q8;
            Q8=makeQuery(id+"F1.opExtrude","CAP_FACE",FACE,{"disambiguationData":[OSD([sQuery(id+"F0.wireOp",EDGE,"E1.bottom"),sQuery(id+"F0.wireOp",EDGE,"E1.top"),sQuery(id+"F0.wireOp",EDGE,"E1.left"),sQuery(id+"F0.wireOp",EDGE,"E1.right")])],"isStart":false});
            extrude(context, id + "F13", {"entities" : qUnion([Q0, Q1, Q2, Q3, Q4, Q5, Q6, Q7]), "endBound" : BoundingType.UP_TO_SURFACE, "depth" : 25.4 * mm, "endBoundEntityFace" : qUnion([Q8]), "offsetDistance" : 25.4 * mm});
        }
    });
